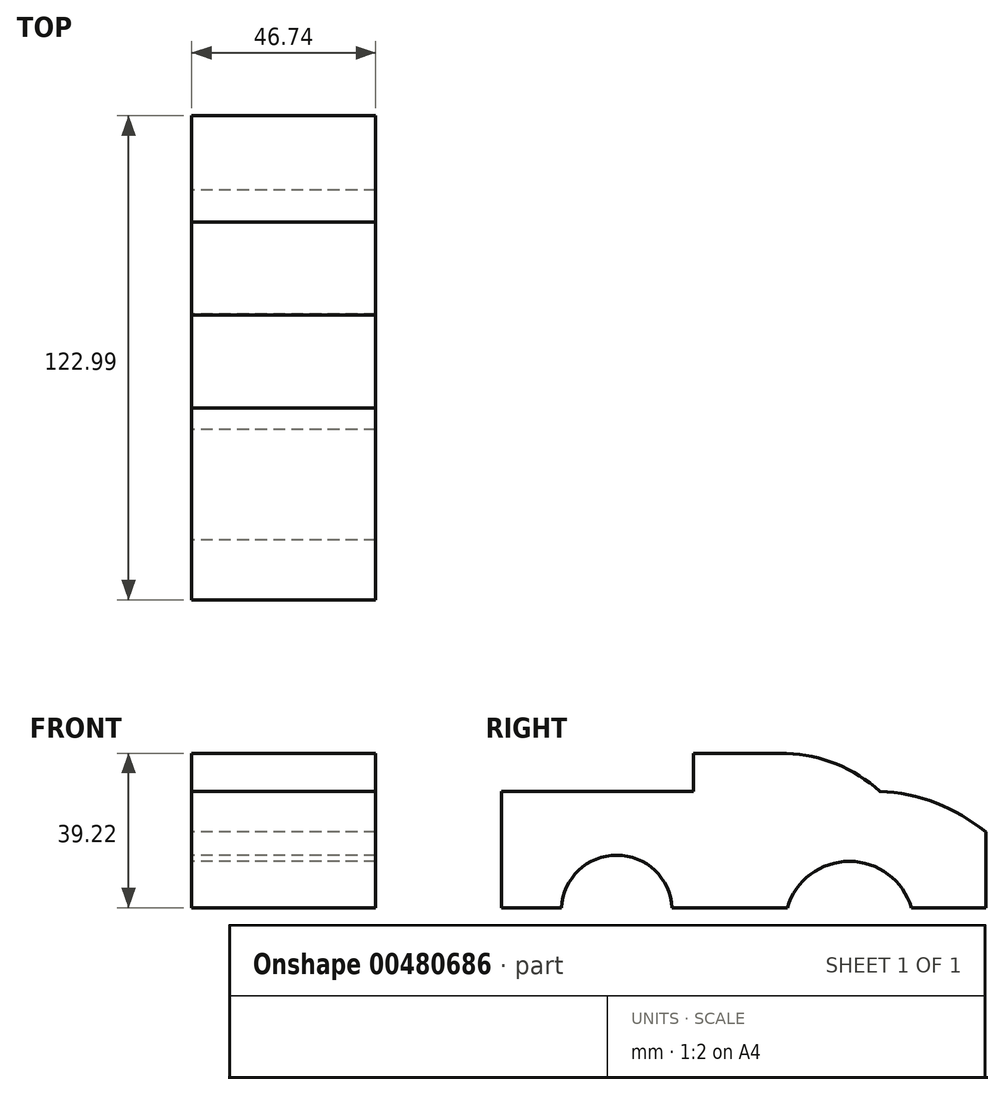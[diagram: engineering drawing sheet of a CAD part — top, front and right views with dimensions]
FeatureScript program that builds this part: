
annotation { "Feature Type Name" : "Feature", "Feature Type Description" : "" }
export const myFeature = defineFeature(function(context is Context, id is Id, definition is map)
    precondition{}
    {
        {
            var Q0;
            Q0=qCreatedBy(makeId("Right.planeOp"),FACE);
            var sketch = newSketch(context, id + "F0", { "sketchPlane" : qUnion([Q0])});
            skLineSegment(sketch, "E0", {"start": v(0, 0) * mm, "end": v(-59.39, 0) * mm});
            skLineSegment(sketch, "E1", {"start": v(-59.39, 0) * mm, "end": v(-59.39, -29.6) * mm});
            skLineSegment(sketch, "E2", {"start": v(-59.39, -29.6) * mm, "end": v(-44.18, -29.6) * mm});
            skArc(sketch, "E3", {"start": v(-16.13, -29.6) * mm, "mid": v(-30.15, -16.25) * mm, "end": v(-44.18, -29.6) * mm});
            skLineSegment(sketch, "E4", {"start": v(-16.13, -29.6) * mm, "end": v(13.2, -29.6) * mm});
            skArc(sketch, "E5", {"start": v(44.72, -29.6) * mm, "mid": v(28.96, -17.83) * mm, "end": v(13.2, -29.6) * mm});
            skLineSegment(sketch, "E6", {"start": v(44.72, -29.6) * mm, "end": v(63.6, -29.6) * mm});
            skLineSegment(sketch, "E7", {"start": v(63.6, -29.6) * mm, "end": v(63.6, -10.36) * mm});
            skArc(sketch, "E8", {"start": v(63.6, -10.36) * mm, "mid": v(50.97, -3) * mm, "end": v(36.66, 0) * mm});
            skArc(sketch, "E9", {"start": v(36.66, 0) * mm, "mid": v(25.69, 6.9) * mm, "end": v(13.01, 9.62) * mm});
            skLineSegment(sketch, "E10", {"start": v(13.01, 9.62) * mm, "end": v(-10.63, 9.62) * mm});
            skLineSegment(sketch, "E11", {"start": v(-10.63, 9.62) * mm, "end": v(-10.63, 0) * mm});
            skLineSegment(sketch, "E12", {"start": v(-10.63, 0) * mm, "end": v(-59.39, 0) * mm});
            skSolve(sketch);
        }
        {
            var Q0;
            Q0=makeQuery(id+"F0.imprint","IMPRINT",FACE,{"disambiguationData":[TD([[makeQuery(id+"F0.imprint","IMPRINT",EDGE,{"derivedFrom":sQuery(id+"F0.wireOp",EDGE,"E1")}),1.0]])]});
            extrude(context, id + "F1", {"entities" : qUnion([Q0]), "depth" : 46.74 * mm});
        }
    });
